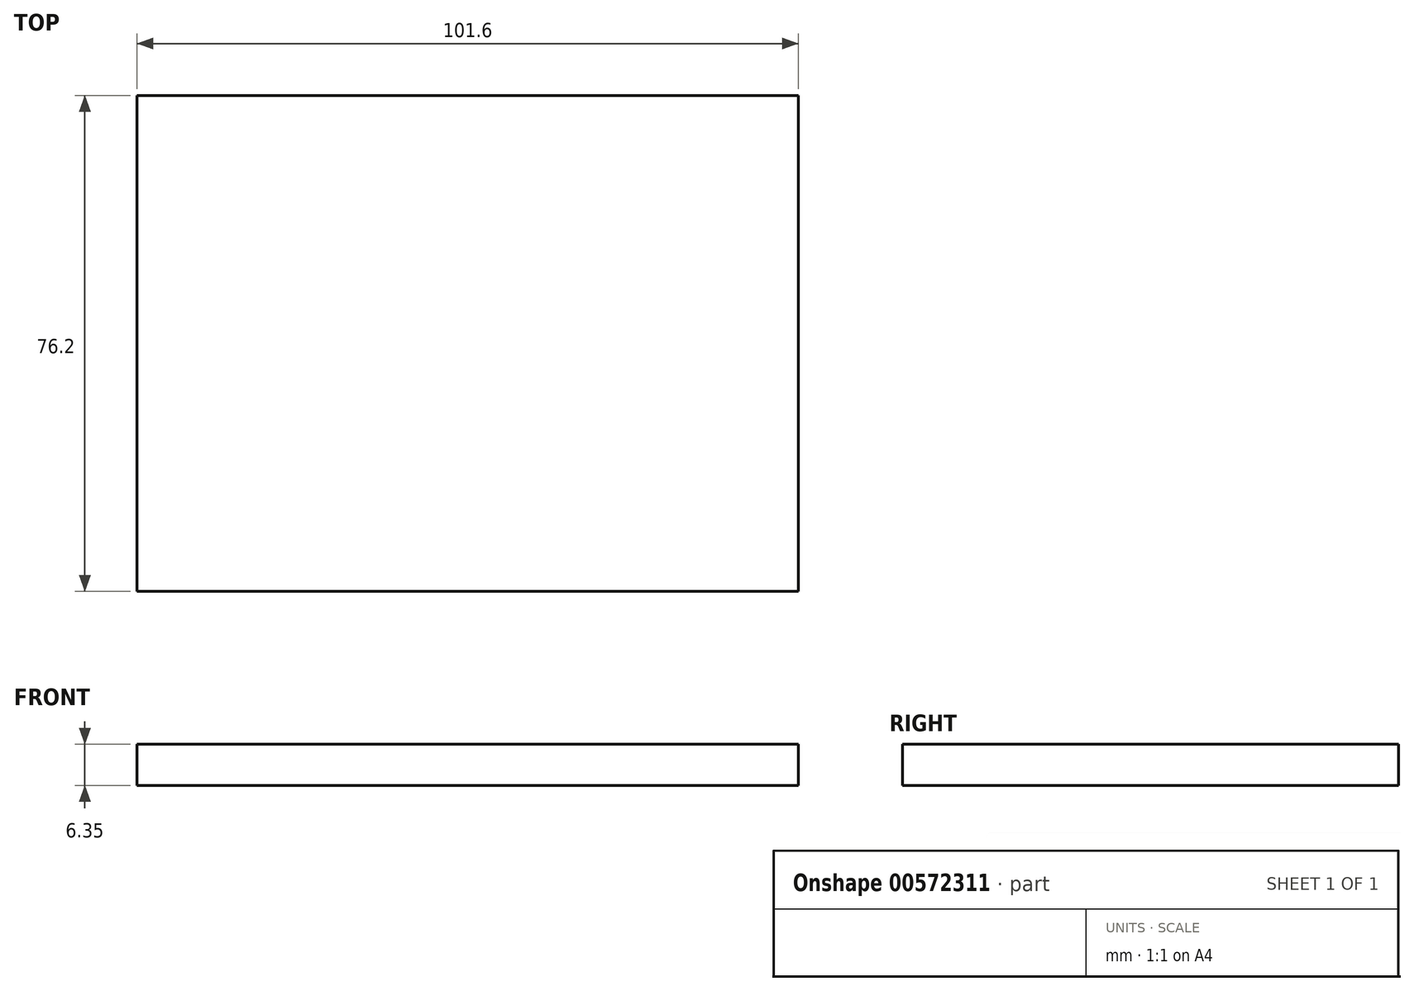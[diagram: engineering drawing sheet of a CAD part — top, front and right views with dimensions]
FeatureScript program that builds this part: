
annotation { "Feature Type Name" : "Feature", "Feature Type Description" : "" }
export const myFeature = defineFeature(function(context is Context, id is Id, definition is map)
    precondition{}
    {
        {
            var Q0;
            Q0=qCreatedBy(makeId("Top.planeOp"),FACE);
            var sketch = newSketch(context, id + "F0", { "sketchPlane" : qUnion([Q0])});
            skLineSegment(sketch, "E0.bottom", {"start": v(-50.8, 38.1) * mm, "end": v(50.8, 38.1) * mm});
            skLineSegment(sketch, "E0.top", {"start": v(-50.8, -38.1) * mm, "end": v(50.8, -38.1) * mm});
            skLineSegment(sketch, "E0.left", {"start": v(-50.8, 38.1) * mm, "end": v(-50.8, -38.1) * mm});
            skLineSegment(sketch, "E0.right", {"start": v(50.8, 38.1) * mm, "end": v(50.8, -38.1) * mm});
            skPoint(sketch, "E0.middle", {"position": v(0, 0) * mm});
            skSolve(sketch);
        }
        {
            var Q0;
            Q0=makeQuery(id+"F0.imprint","IMPRINT",FACE,{"disambiguationData":[TD([[makeQuery(id+"F0.imprint","IMPRINT",EDGE,{"derivedFrom":sQuery(id+"F0.wireOp",EDGE,"E0.bottom")}),-1.0]])]});
            extrude(context, id + "F1", {"entities" : qUnion([Q0]), "depth" : 6.35 * mm, "offsetDistance" : 25.4 * mm});
        }
    });
